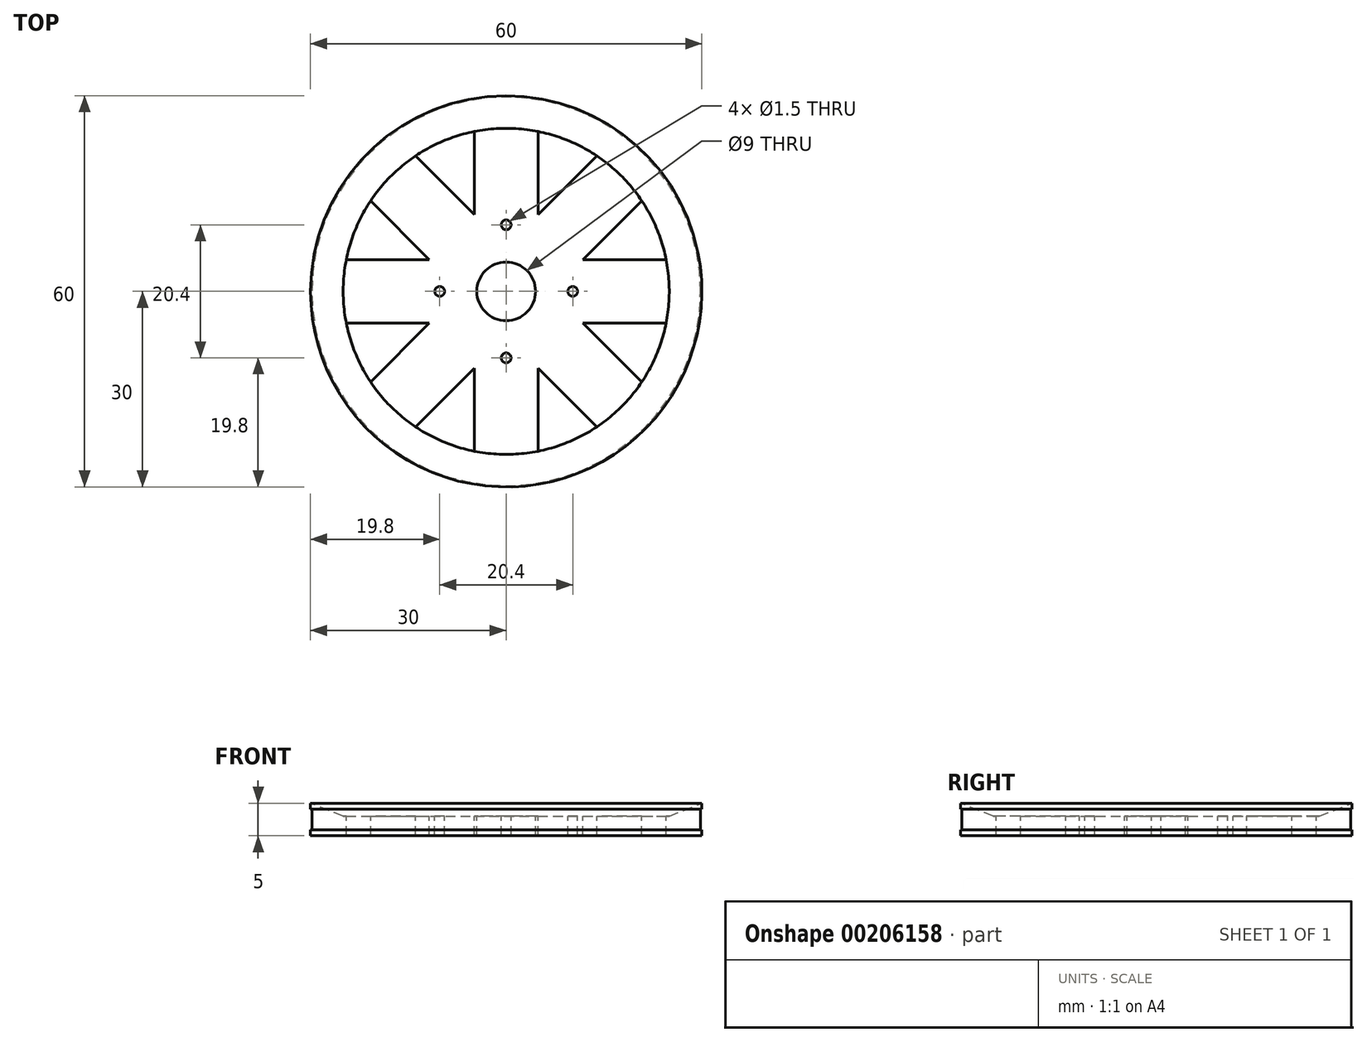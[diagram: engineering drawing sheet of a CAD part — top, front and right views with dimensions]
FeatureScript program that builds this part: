
annotation { "Feature Type Name" : "Feature", "Feature Type Description" : "" }
export const myFeature = defineFeature(function(context is Context, id is Id, definition is map)
    precondition{}
    {
        {
            var Q0;
            Q0=qCreatedBy(makeId("Top.planeOp"),FACE);
            var sketch = newSketch(context, id + "F0", { "sketchPlane" : qUnion([Q0])});
            skCircle(sketch, "E0", {"center": v(0, 0) * mm, "radius": 30 * mm});
            skSolve(sketch);
        }
        {
            var Q0;
            Q0 = qSketchRegion(id + "F0", true);
            extrude(context, id + "F1", {"entities" : qUnion([Q0]), "depth" : 3 * mm});
        }
        {
            var Q0;
            Q0=makeQuery(id+"F1.opExtrude","CAP_FACE",FACE,{"disambiguationData":[OSD([sQuery(id+"F0.wireOp",EDGE,"E0")])],"isStart":false});
            var sketch = newSketch(context, id + "F2", { "sketchPlane" : qUnion([Q0])});
            skCircle(sketch, "E1", {"center": v(0, 0) * mm, "radius": 4.5 * mm});
            skCircle(sketch, "E2", {"center": v(-10.2, 0) * mm, "radius": 0.75 * mm});
            skCircle(sketch, "E3", {"center": v(10.2, 0) * mm, "radius": 0.75 * mm});
            skCircle(sketch, "E4", {"center": v(0, 10.2) * mm, "radius": 0.75 * mm});
            skCircle(sketch, "E5", {"center": v(0, -10.2) * mm, "radius": 0.75 * mm});
            skLineSegment(sketch, "E6", {"start": v(-10.2, 0) * mm, "end": v(10.2, 0) * mm, "construction": true});
            skLineSegment(sketch, "E7", {"start": v(0, 10.2) * mm, "end": v(0, -10.2) * mm, "construction": true});
            skArc(sketch, "E8", {"start": v(-4.88, 24.52) * mm, "mid": v(-9.57, 23.1) * mm, "end": v(-13.89, 20.79) * mm});
            skLineSegment(sketch, "E9", {"start": v(-4.88, 24.52) * mm, "end": v(-4.88, 11.77) * mm});
            skLineSegment(sketch, "E10", {"start": v(4.88, 24.52) * mm, "end": v(4.88, 11.77) * mm});
            skLineSegment(sketch, "E11", {"start": v(-24.52, 4.88) * mm, "end": v(-11.77, 4.88) * mm});
            skLineSegment(sketch, "E12", {"start": v(-24.52, -4.88) * mm, "end": v(-11.77, -4.88) * mm});
            skLineSegment(sketch, "E13", {"start": v(-20.79, 13.89) * mm, "end": v(-11.77, 4.88) * mm});
            skLineSegment(sketch, "E14", {"start": v(-13.89, 20.79) * mm, "end": v(-4.88, 11.77) * mm});
            skLineSegment(sketch, "E15", {"start": v(-20.79, -13.89) * mm, "end": v(-11.77, -4.88) * mm});
            skLineSegment(sketch, "E16", {"start": v(-13.89, -20.79) * mm, "end": v(-4.88, -11.77) * mm});
            skArc(sketch, "E17.trimOffspring", {"start": v(-20.79, 13.89) * mm, "mid": v(-23.1, 9.57) * mm, "end": v(-24.52, 4.88) * mm});
            skArc(sketch, "E18.trimOffspring", {"start": v(-24.52, -4.88) * mm, "mid": v(-23.1, -9.57) * mm, "end": v(-20.79, -13.89) * mm});
            skArc(sketch, "E19.trimOffspring", {"start": v(-13.89, -20.79) * mm, "mid": v(-9.57, -23.1) * mm, "end": v(-4.88, -24.52) * mm});
            skArc(sketch, "E20.trimOffspring", {"start": v(4.88, -24.52) * mm, "mid": v(9.57, -23.1) * mm, "end": v(13.89, -20.79) * mm});
            skArc(sketch, "E21.trimOffspring", {"start": v(20.79, -13.89) * mm, "mid": v(23.1, -9.57) * mm, "end": v(24.52, -4.88) * mm});
            skArc(sketch, "E22.trimOffspring", {"start": v(24.52, 4.88) * mm, "mid": v(23.1, 9.57) * mm, "end": v(20.79, 13.89) * mm});
            skArc(sketch, "E23.trimOffspring", {"start": v(13.89, 20.79) * mm, "mid": v(9.57, 23.1) * mm, "end": v(4.88, 24.52) * mm});
            skLineSegment(sketch, "E24.trimOffspring", {"start": v(4.88, 11.77) * mm, "end": v(13.89, 20.79) * mm});
            skLineSegment(sketch, "E25.trimOffspring", {"start": v(-4.88, -11.77) * mm, "end": v(-4.88, -24.52) * mm});
            skLineSegment(sketch, "E26.trimOffspring", {"start": v(4.88, -11.77) * mm, "end": v(13.89, -20.79) * mm});
            skLineSegment(sketch, "E27.trimOffspring", {"start": v(4.88, -11.77) * mm, "end": v(4.88, -24.52) * mm});
            skLineSegment(sketch, "E28.trimOffspring", {"start": v(11.77, -4.88) * mm, "end": v(24.52, -4.88) * mm});
            skLineSegment(sketch, "E29.trimOffspring", {"start": v(11.77, -4.88) * mm, "end": v(20.79, -13.89) * mm});
            skLineSegment(sketch, "E30.trimOffspring", {"start": v(11.77, 4.88) * mm, "end": v(24.52, 4.88) * mm});
            skLineSegment(sketch, "E31.trimOffspring", {"start": v(11.77, 4.88) * mm, "end": v(20.79, 13.89) * mm});
            skLineSegment(sketch, "E32", {"start": v(-13.89, 20.79) * mm, "end": v(-4.88, 24.52) * mm, "construction": true});
            skLineSegment(sketch, "E33", {"start": v(-4.88, 24.52) * mm, "end": v(4.88, 24.52) * mm, "construction": true});
            skLineSegment(sketch, "E34", {"start": v(4.88, 24.52) * mm, "end": v(13.89, 20.79) * mm, "construction": true});
            skLineSegment(sketch, "E35", {"start": v(13.89, 20.79) * mm, "end": v(20.79, 13.89) * mm, "construction": true});
            skLineSegment(sketch, "E36", {"start": v(20.79, 13.89) * mm, "end": v(24.52, 4.88) * mm, "construction": true});
            skLineSegment(sketch, "E37", {"start": v(24.52, 4.88) * mm, "end": v(24.52, -4.88) * mm, "construction": true});
            skLineSegment(sketch, "E38", {"start": v(24.52, -4.88) * mm, "end": v(20.79, -13.89) * mm, "construction": true});
            skLineSegment(sketch, "E39", {"start": v(20.79, -13.89) * mm, "end": v(13.89, -20.79) * mm, "construction": true});
            skLineSegment(sketch, "E40", {"start": v(13.89, -20.79) * mm, "end": v(4.88, -24.52) * mm, "construction": true});
            skLineSegment(sketch, "E41", {"start": v(4.88, -24.52) * mm, "end": v(-4.88, -24.52) * mm, "construction": true});
            skLineSegment(sketch, "E42", {"start": v(-4.88, -24.52) * mm, "end": v(-13.89, -20.79) * mm, "construction": true});
            skLineSegment(sketch, "E43", {"start": v(-13.89, -20.79) * mm, "end": v(-20.79, -13.89) * mm, "construction": true});
            skLineSegment(sketch, "E44", {"start": v(-20.79, -13.89) * mm, "end": v(-24.52, -4.88) * mm, "construction": true});
            skLineSegment(sketch, "E45", {"start": v(-24.52, -4.88) * mm, "end": v(-24.52, 4.88) * mm, "construction": true});
            skLineSegment(sketch, "E46", {"start": v(-24.52, 4.88) * mm, "end": v(-20.79, 13.89) * mm, "construction": true});
            skLineSegment(sketch, "E47", {"start": v(-20.79, 13.89) * mm, "end": v(-13.89, 20.79) * mm, "construction": true});
            skSolve(sketch);
        }
        {
            var Q0;
            Q0 = qSketchRegion(id + "F2", true);
            extrude(context, id + "F3", {"entities" : qUnion([Q0]), "operationType" : NewBodyOperationType.REMOVE, "oppositeDirection" : true, "depth" : 25 * mm});
        }
        {
            var Q0;
            Q0=qCreatedBy(makeId("Front.planeOp"),FACE);
            var sketch = newSketch(context, id + "F4", { "sketchPlane" : qUnion([Q0])});
            skLineSegment(sketch, "E48.0", {"start": v(-30, 3) * mm, "end": v(-25, 3) * mm});
            skLineSegment(sketch, "E49", {"start": v(-30, 3) * mm, "end": v(-30, 5) * mm});
            skLineSegment(sketch, "E50", {"start": v(-30, 5) * mm, "end": v(-25, 3) * mm});
            skPoint(sketch, "E51.orphan", {"position": v(30, 3) * mm});
            skSolve(sketch);
        }
        {
            var Q0;
            Q0 = qSketchRegion(id + "F4", true);
            var Q1;
            Q1=makeQuery(id+"F1.opExtrude","CAP_EDGE",EDGE,{"disambiguationData":[OSD([sQuery(id+"F0.wireOp",EDGE,"E0")])],"isStart":false});
            revolve(context, id + "F5", {"operationType" : NewBodyOperationType.ADD, "entities" : qUnion([Q0]), "axis" : qUnion([Q1]), "revolveType" : RevolveType.FULL});
        }
        {
            var Q0;
            Q0=qCreatedBy(makeId("Front.planeOp"),FACE);
            var sketch = newSketch(context, id + "F6", { "sketchPlane" : qUnion([Q0])});
            skLineSegment(sketch, "E52.bottom", {"start": v(-30, 4.1) * mm, "end": v(-29.8, 4.1) * mm});
            skLineSegment(sketch, "E52.top", {"start": v(-30, 0.9) * mm, "end": v(-29.8, 0.9) * mm});
            skLineSegment(sketch, "E52.left", {"start": v(-30, 4.1) * mm, "end": v(-30, 0.9) * mm});
            skLineSegment(sketch, "E52.right", {"start": v(-29.8, 4.1) * mm, "end": v(-29.8, 0.9) * mm});
            skLineSegment(sketch, "E53", {"start": v(-30, 4.1) * mm, "end": v(-30, 5) * mm, "construction": true});
            skLineSegment(sketch, "E54", {"start": v(-30, 0.9) * mm, "end": v(-30, 0) * mm, "construction": true});
            skSolve(sketch);
        }
        {
            var Q0;
            Q0 = qSketchRegion(id + "F6", true);
            var Q1;
            Q1=makeQuery(id+"F5.opRevolve","SWEPT_EDGE",EDGE,{"disambiguationData":[OSD([sQuery(id+"F4.wireOp",EDGE,"E49"),sQuery(id+"F4.wireOp",EDGE,"E50")])]});
            revolve(context, id + "F7", {"operationType" : NewBodyOperationType.REMOVE, "entities" : qUnion([Q0]), "axis" : qUnion([Q1]), "revolveType" : RevolveType.FULL, "oppositeDirection" : true});
        }
    });
